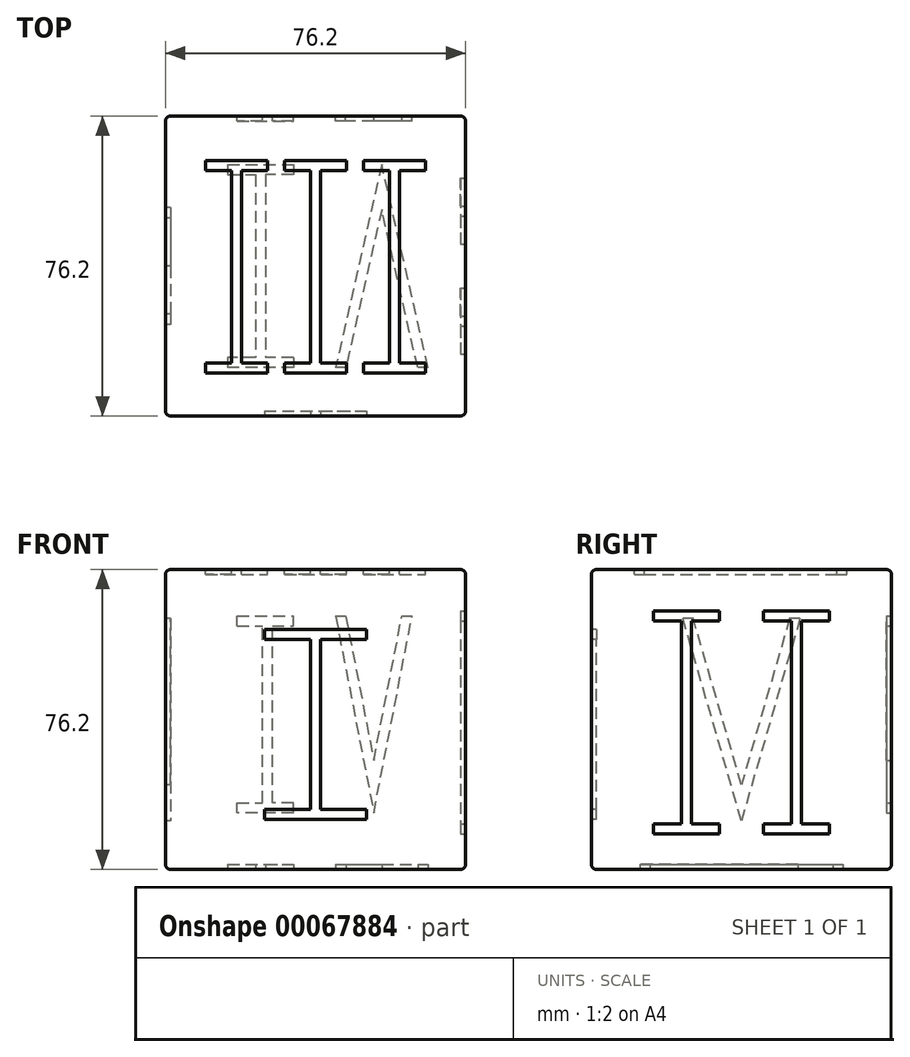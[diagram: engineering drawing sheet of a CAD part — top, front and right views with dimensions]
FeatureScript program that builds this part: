
annotation { "Feature Type Name" : "Feature", "Feature Type Description" : "" }
export const myFeature = defineFeature(function(context is Context, id is Id, definition is map)
    precondition{}
    {
        {
            var Q0;
            Q0=qCreatedBy(makeId("Top.planeOp"),FACE);
            var sketch = newSketch(context, id + "F0", { "sketchPlane" : qUnion([Q0])});
            skLineSegment(sketch, "E0.rect.bottom", {"start": v(38.1, -38.1) * mm, "end": v(-38.1, -38.1) * mm});
            skLineSegment(sketch, "E0.rect.top", {"start": v(38.1, 38.1) * mm, "end": v(-38.1, 38.1) * mm});
            skLineSegment(sketch, "E0.rect.left", {"start": v(38.1, -38.1) * mm, "end": v(38.1, 38.1) * mm});
            skLineSegment(sketch, "E0.rect.right", {"start": v(-38.1, -38.1) * mm, "end": v(-38.1, 38.1) * mm});
            skPoint(sketch, "E0.rect.middle", {"position": v(0, 0) * mm});
            skSolve(sketch);
        }
        {
            var Q0;
            Q0=makeQuery(id+"F0.imprint","IMPRINT",FACE,{"disambiguationData":[TD([[makeQuery(id+"F0.imprint","IMPRINT",EDGE,{"derivedFrom":sQuery(id+"F0.wireOp",EDGE,"E0.rect.bottom")}),-1.0]])]});
            extrude(context, id + "F1", {"entities" : qUnion([Q0]), "endBound" : BoundingType.SYMMETRIC, "depth" : 76.2 * mm});
        }
        {
            var Q0;
            Q0=makeQuery(id+"F1.opExtrude","SWEPT_FACE",FACE,{"disambiguationData":[OSD([sQuery(id+"F0.wireOp",EDGE,"E0.rect.bottom")])]});
            var sketch = newSketch(context, id + "F2", { "sketchPlane" : qUnion([Q0])});
            skLineSegment(sketch, "E1", {"start": v(-13, 22.9) * mm, "end": v(0, 22.9) * mm});
            skLineSegment(sketch, "E2", {"start": v(0, 22.9) * mm, "end": v(13, 22.9) * mm});
            skLineSegment(sketch, "E3", {"start": v(0, 22.9) * mm, "end": v(0, 0) * mm, "construction": true});
            skLineSegment(sketch, "E4.MirrorCS", {"start": v(-13, -22.9) * mm, "end": v(0, -22.9) * mm});
            skLineSegment(sketch, "E5.MirrorCS", {"start": v(0, -22.9) * mm, "end": v(13, -22.9) * mm});
            skLineSegment(sketch, "E6.MirrorCS", {"start": v(0, -22.9) * mm, "end": v(0, 0) * mm, "construction": true});
            skLineSegment(sketch, "E7.0", {"start": v(0, 20.36) * mm, "end": v(13, 20.36) * mm});
            skLineSegment(sketch, "E7.1", {"start": v(-13, 20.36) * mm, "end": v(0, 20.36) * mm});
            skLineSegment(sketch, "E8.0", {"start": v(0, -25.44) * mm, "end": v(13, -25.44) * mm});
            skLineSegment(sketch, "E8.1", {"start": v(-13, -25.44) * mm, "end": v(0, -25.44) * mm});
            skLineSegment(sketch, "E9.0", {"start": v(-1.27, -22.9) * mm, "end": v(-1.27, 0) * mm});
            skLineSegment(sketch, "E9.1", {"start": v(-1.27, 22.9) * mm, "end": v(-1.27, 0) * mm});
            skLineSegment(sketch, "E10.0", {"start": v(1.27, -22.9) * mm, "end": v(1.27, 0) * mm});
            skLineSegment(sketch, "E10.1", {"start": v(1.27, 22.9) * mm, "end": v(1.27, 0) * mm});
            skLineSegment(sketch, "E11", {"start": v(-13, 22.9) * mm, "end": v(-13, 20.36) * mm});
            skLineSegment(sketch, "E12", {"start": v(13, 22.9) * mm, "end": v(13, 20.36) * mm});
            skLineSegment(sketch, "E13", {"start": v(13, -22.9) * mm, "end": v(13, -25.44) * mm});
            skLineSegment(sketch, "E14", {"start": v(-13, -25.44) * mm, "end": v(-13, -22.9) * mm});
            skSolve(sketch);
        }
        {
            var Q0;
            Q0 = qSketchRegion(id + "F2", true);
            extrude(context, id + "F3", {"entities" : qUnion([Q0]), "operationType" : NewBodyOperationType.REMOVE, "endBound" : BoundingType.SYMMETRIC, "oppositeDirection" : true, "depth" : 2.54 * mm});
        }
        {
            var Q0;
            Q0=makeQuery(id+"F1.opExtrude","SWEPT_FACE",FACE,{"disambiguationData":[OSD([sQuery(id+"F0.wireOp",EDGE,"E0.rect.top")])]});
            var sketch = newSketch(context, id + "F4", { "sketchPlane" : qUnion([Q0])});
            skLineSegment(sketch, "E15", {"start": v(-23.23, 26.29) * mm, "end": v(-14.8, -17.08) * mm, "construction": true});
            skLineSegment(sketch, "E16", {"start": v(-14.8, -17.08) * mm, "end": v(-6.37, 26.29) * mm, "construction": true});
            skLineSegment(sketch, "E17", {"start": v(5.59, 23.75) * mm, "end": v(12.23, 23.75) * mm});
            skLineSegment(sketch, "E18", {"start": v(12.23, 23.75) * mm, "end": v(19.96, 23.75) * mm});
            skLineSegment(sketch, "E19", {"start": v(12.23, 23.75) * mm, "end": v(12.23, -21.2) * mm, "construction": true});
            skLineSegment(sketch, "E20", {"start": v(12.23, -21.2) * mm, "end": v(5.59, -21.2) * mm});
            skLineSegment(sketch, "E21", {"start": v(12.23, -21.2) * mm, "end": v(19.96, -21.2) * mm});
            skLineSegment(sketch, "E22.0", {"start": v(-14.8, -10.43) * mm, "end": v(-7.67, 26.29) * mm});
            skLineSegment(sketch, "E22.1", {"start": v(-21.94, 26.29) * mm, "end": v(-14.8, -10.43) * mm});
            skLineSegment(sketch, "E23.0", {"start": v(12.23, 26.29) * mm, "end": v(19.96, 26.29) * mm});
            skLineSegment(sketch, "E23.1", {"start": v(5.59, 26.29) * mm, "end": v(12.23, 26.29) * mm});
            skLineSegment(sketch, "E24.0", {"start": v(12.23, -23.74) * mm, "end": v(5.59, -23.74) * mm});
            skLineSegment(sketch, "E24.1", {"start": v(12.23, -23.74) * mm, "end": v(19.96, -23.74) * mm});
            skLineSegment(sketch, "E25.0", {"start": v(10.96, 23.75) * mm, "end": v(10.96, -21.2) * mm});
            skLineSegment(sketch, "E26.0", {"start": v(13.5, 23.75) * mm, "end": v(13.5, -21.2) * mm});
            skLineSegment(sketch, "E27", {"start": v(5.59, 26.29) * mm, "end": v(5.59, 23.75) * mm});
            skLineSegment(sketch, "E28", {"start": v(19.96, 26.29) * mm, "end": v(19.96, 23.75) * mm});
            skLineSegment(sketch, "E29", {"start": v(19.96, -21.2) * mm, "end": v(19.96, -23.74) * mm});
            skLineSegment(sketch, "E30", {"start": v(5.59, -21.2) * mm, "end": v(5.59, -23.74) * mm});
            skLineSegment(sketch, "E31.0", {"start": v(-14.8, -23.74) * mm, "end": v(-5.08, 26.29) * mm});
            skLineSegment(sketch, "E31.1", {"start": v(-24.53, 26.29) * mm, "end": v(-14.8, -23.74) * mm});
            skLineSegment(sketch, "E32", {"start": v(-24.53, 26.29) * mm, "end": v(-21.94, 26.29) * mm});
            skLineSegment(sketch, "E33", {"start": v(-7.67, 26.29) * mm, "end": v(-5.08, 26.29) * mm});
            skSolve(sketch);
        }
        {
            var Q0;
            Q0 = qSketchRegion(id + "F4", true);
            extrude(context, id + "F5", {"entities" : qUnion([Q0]), "operationType" : NewBodyOperationType.REMOVE, "endBound" : BoundingType.SYMMETRIC, "oppositeDirection" : true, "depth" : 2.54 * mm});
        }
        {
            var Q0;
            Q0=makeQuery(id+"F1.opExtrude","SWEPT_FACE",FACE,{"disambiguationData":[OSD([sQuery(id+"F0.wireOp",EDGE,"E0.rect.right")])]});
            var sketch = newSketch(context, id + "F6", { "sketchPlane" : qUnion([Q0])});
            skLineSegment(sketch, "E34", {"start": v(-12.58, 22.26) * mm, "end": v(0, -21.16) * mm, "construction": true});
            skLineSegment(sketch, "E35", {"start": v(0, -21.16) * mm, "end": v(12.58, 22.26) * mm, "construction": true});
            skLineSegment(sketch, "E36.0", {"start": v(0, -25.72) * mm, "end": v(14.89, 25.65) * mm});
            skLineSegment(sketch, "E36.1", {"start": v(-14.89, 25.65) * mm, "end": v(0, -25.72) * mm});
            skLineSegment(sketch, "E37.0", {"start": v(0, -16.6) * mm, "end": v(12.24, 25.65) * mm});
            skLineSegment(sketch, "E37.1", {"start": v(-12.24, 25.65) * mm, "end": v(0, -16.6) * mm});
            skLineSegment(sketch, "E38", {"start": v(-14.89, 25.65) * mm, "end": v(-12.24, 25.65) * mm});
            skLineSegment(sketch, "E39", {"start": v(12.24, 25.65) * mm, "end": v(14.89, 25.65) * mm});
            skSolve(sketch);
        }
        {
            var Q0;
            Q0 = qSketchRegion(id + "F6", true);
            extrude(context, id + "F7", {"entities" : qUnion([Q0]), "operationType" : NewBodyOperationType.REMOVE, "endBound" : BoundingType.SYMMETRIC, "oppositeDirection" : true, "depth" : 2.54 * mm});
        }
        {
            var Q0;
            Q0=makeQuery(id+"F1.opExtrude","SWEPT_FACE",FACE,{"disambiguationData":[OSD([sQuery(id+"F0.wireOp",EDGE,"E0.rect.left")])]});
            var sketch = newSketch(context, id + "F8", { "sketchPlane" : qUnion([Q0])});
            skLineSegment(sketch, "E40", {"start": v(-22.35, 24.97) * mm, "end": v(-13.97, 24.97) * mm});
            skLineSegment(sketch, "E41", {"start": v(-13.97, 24.97) * mm, "end": v(-5.59, 24.97) * mm});
            skLineSegment(sketch, "E42", {"start": v(-13.97, 24.97) * mm, "end": v(-13.97, -26.48) * mm, "construction": true});
            skLineSegment(sketch, "E43", {"start": v(-13.97, -26.48) * mm, "end": v(-22.35, -26.48) * mm});
            skLineSegment(sketch, "E44", {"start": v(-13.97, -26.48) * mm, "end": v(-5.59, -26.48) * mm});
            skLineSegment(sketch, "E45.0", {"start": v(-13.97, 27.51) * mm, "end": v(-5.59, 27.51) * mm});
            skLineSegment(sketch, "E45.1", {"start": v(-22.35, 27.51) * mm, "end": v(-13.97, 27.51) * mm});
            skLineSegment(sketch, "E46.0", {"start": v(-13.97, -29.02) * mm, "end": v(-22.35, -29.02) * mm});
            skLineSegment(sketch, "E46.1", {"start": v(-13.97, -29.02) * mm, "end": v(-5.59, -29.02) * mm});
            skLineSegment(sketch, "E47.0", {"start": v(-15.24, 24.97) * mm, "end": v(-15.24, -26.48) * mm});
            skLineSegment(sketch, "E48.0", {"start": v(-12.7, 24.97) * mm, "end": v(-12.7, -26.48) * mm});
            skLineSegment(sketch, "E49", {"start": v(-22.35, 27.51) * mm, "end": v(-22.35, 24.97) * mm});
            skLineSegment(sketch, "E50", {"start": v(-5.59, 27.51) * mm, "end": v(-5.59, 24.97) * mm});
            skLineSegment(sketch, "E51", {"start": v(-22.35, -29.02) * mm, "end": v(-22.35, -26.48) * mm});
            skLineSegment(sketch, "E52", {"start": v(-5.59, -26.48) * mm, "end": v(-5.59, -29.02) * mm});
            skLineSegment(sketch, "E53.MirrorCS", {"start": v(12.7, 24.97) * mm, "end": v(12.7, -26.48) * mm});
            skLineSegment(sketch, "E54.MirrorCS", {"start": v(13.97, 24.97) * mm, "end": v(5.59, 24.97) * mm});
            skLineSegment(sketch, "E55.MirrorCS", {"start": v(5.59, 27.51) * mm, "end": v(5.59, 24.97) * mm});
            skLineSegment(sketch, "E56.MirrorCS", {"start": v(13.97, 27.51) * mm, "end": v(5.59, 27.51) * mm});
            skLineSegment(sketch, "E57.MirrorCS", {"start": v(22.35, 27.51) * mm, "end": v(13.97, 27.51) * mm});
            skLineSegment(sketch, "E58.MirrorCS", {"start": v(22.35, 27.51) * mm, "end": v(22.35, 24.97) * mm});
            skLineSegment(sketch, "E59.MirrorCS", {"start": v(15.24, 24.97) * mm, "end": v(15.24, -26.48) * mm});
            skLineSegment(sketch, "E60.MirrorCS", {"start": v(13.97, -26.48) * mm, "end": v(22.35, -26.48) * mm});
            skLineSegment(sketch, "E61.MirrorCS", {"start": v(13.97, -26.48) * mm, "end": v(5.59, -26.48) * mm});
            skLineSegment(sketch, "E62.MirrorCS", {"start": v(13.97, -29.02) * mm, "end": v(5.59, -29.02) * mm});
            skLineSegment(sketch, "E63.MirrorCS", {"start": v(5.59, -26.48) * mm, "end": v(5.59, -29.02) * mm});
            skLineSegment(sketch, "E64.MirrorCS", {"start": v(22.35, -29.02) * mm, "end": v(22.35, -26.48) * mm});
            skLineSegment(sketch, "E65.MirrorCS", {"start": v(13.97, -29.02) * mm, "end": v(22.35, -29.02) * mm});
            skLineSegment(sketch, "E66.MirrorCS", {"start": v(22.35, 24.97) * mm, "end": v(13.97, 24.97) * mm});
            skSolve(sketch);
        }
        {
            var Q0;
            Q0 = qSketchRegion(id + "F8", true);
            extrude(context, id + "F9", {"entities" : qUnion([Q0]), "operationType" : NewBodyOperationType.REMOVE, "endBound" : BoundingType.SYMMETRIC, "oppositeDirection" : true, "depth" : 2.54 * mm});
        }
        {
            var Q0;
            Q0=makeQuery(id+"F1.opExtrude","CAP_FACE",FACE,{"disambiguationData":[OSD([sQuery(id+"F0.wireOp",EDGE,"E0.rect.bottom"),sQuery(id+"F0.wireOp",EDGE,"E0.rect.top"),sQuery(id+"F0.wireOp",EDGE,"E0.rect.left"),sQuery(id+"F0.wireOp",EDGE,"E0.rect.right")])],"isStart":true});
            var sketch = newSketch(context, id + "F10", { "sketchPlane" : qUnion([Q0])});
            skLineSegment(sketch, "E67", {"start": v(-22.35, 23.28) * mm, "end": v(-13.97, 23.28) * mm});
            skLineSegment(sketch, "E68", {"start": v(-13.97, 23.28) * mm, "end": v(-5.59, 23.28) * mm});
            skLineSegment(sketch, "E69", {"start": v(-13.97, -23.2) * mm, "end": v(-22.35, -23.2) * mm});
            skLineSegment(sketch, "E70", {"start": v(-13.97, -23.2) * mm, "end": v(-5.59, -23.2) * mm});
            skLineSegment(sketch, "E71", {"start": v(-13.97, 23.28) * mm, "end": v(-13.97, -23.2) * mm, "construction": true});
            skLineSegment(sketch, "E72", {"start": v(6.38, 25.82) * mm, "end": v(16.83, -20.02) * mm, "construction": true});
            skLineSegment(sketch, "E73", {"start": v(16.83, -20.02) * mm, "end": v(27.28, 25.82) * mm, "construction": true});
            skLineSegment(sketch, "E74.0", {"start": v(-13.97, 25.82) * mm, "end": v(-5.59, 25.82) * mm});
            skLineSegment(sketch, "E74.1", {"start": v(-22.35, 25.82) * mm, "end": v(-13.97, 25.82) * mm});
            skLineSegment(sketch, "E75.0", {"start": v(-13.97, -25.73) * mm, "end": v(-22.35, -25.73) * mm});
            skLineSegment(sketch, "E75.1", {"start": v(-13.97, -25.73) * mm, "end": v(-5.59, -25.73) * mm});
            skLineSegment(sketch, "E76.0", {"start": v(-15.24, 23.28) * mm, "end": v(-15.24, -23.2) * mm});
            skLineSegment(sketch, "E77.0", {"start": v(-12.7, 23.28) * mm, "end": v(-12.7, -23.2) * mm});
            skLineSegment(sketch, "E78.0", {"start": v(16.83, -25.73) * mm, "end": v(28.58, 25.82) * mm});
            skLineSegment(sketch, "E78.1", {"start": v(5.08, 25.82) * mm, "end": v(16.83, -25.73) * mm});
            skLineSegment(sketch, "E79.0", {"start": v(16.83, -14.3) * mm, "end": v(25.97, 25.82) * mm});
            skLineSegment(sketch, "E79.1", {"start": v(7.69, 25.82) * mm, "end": v(16.83, -14.3) * mm});
            skLineSegment(sketch, "E80", {"start": v(-22.35, 25.82) * mm, "end": v(-22.35, 23.28) * mm});
            skLineSegment(sketch, "E81", {"start": v(-5.59, 25.82) * mm, "end": v(-5.59, 23.28) * mm});
            skLineSegment(sketch, "E82", {"start": v(-22.35, -23.2) * mm, "end": v(-22.35, -25.73) * mm});
            skLineSegment(sketch, "E83", {"start": v(-5.59, -23.2) * mm, "end": v(-5.59, -25.73) * mm});
            skLineSegment(sketch, "E84", {"start": v(5.08, 25.82) * mm, "end": v(7.69, 25.82) * mm});
            skLineSegment(sketch, "E85", {"start": v(25.97, 25.82) * mm, "end": v(28.58, 25.82) * mm});
            skSolve(sketch);
        }
        {
            var Q0;
            Q0 = qSketchRegion(id + "F10", true);
            extrude(context, id + "F11", {"entities" : qUnion([Q0]), "operationType" : NewBodyOperationType.REMOVE, "endBound" : BoundingType.SYMMETRIC, "oppositeDirection" : true, "depth" : 2.54 * mm});
        }
        {
            var Q0;
            Q0=makeQuery(id+"F1.opExtrude","CAP_FACE",FACE,{"disambiguationData":[OSD([sQuery(id+"F0.wireOp",EDGE,"E0.rect.bottom"),sQuery(id+"F0.wireOp",EDGE,"E0.rect.top"),sQuery(id+"F0.wireOp",EDGE,"E0.rect.left"),sQuery(id+"F0.wireOp",EDGE,"E0.rect.right")])],"isStart":false});
            var sketch = newSketch(context, id + "F12", { "sketchPlane" : qUnion([Q0])});
            skLineSegment(sketch, "E86", {"start": v(27.9, -24.69) * mm, "end": v(20.05, -24.69) * mm});
            skLineSegment(sketch, "E87", {"start": v(20.05, -24.69) * mm, "end": v(12.22, -24.69) * mm});
            skLineSegment(sketch, "E88", {"start": v(20.05, -24.69) * mm, "end": v(20.05, 24.25) * mm, "construction": true});
            skLineSegment(sketch, "E89", {"start": v(20.05, 24.25) * mm, "end": v(27.9, 24.25) * mm});
            skLineSegment(sketch, "E90", {"start": v(20.05, 24.25) * mm, "end": v(12.22, 24.25) * mm});
            skLineSegment(sketch, "E91", {"start": v(7.84, -24.69) * mm, "end": v(0, -24.69) * mm});
            skLineSegment(sketch, "E92", {"start": v(0, -24.69) * mm, "end": v(0, 24.25) * mm, "construction": true});
            skLineSegment(sketch, "E93", {"start": v(0, 24.25) * mm, "end": v(7.84, 24.25) * mm});
            skLineSegment(sketch, "E94.0", {"start": v(20.05, -27.23) * mm, "end": v(12.22, -27.23) * mm});
            skLineSegment(sketch, "E94.1", {"start": v(27.9, -27.23) * mm, "end": v(20.05, -27.23) * mm});
            skLineSegment(sketch, "E95.0", {"start": v(20.05, 26.79) * mm, "end": v(27.9, 26.79) * mm});
            skLineSegment(sketch, "E95.1", {"start": v(20.05, 26.79) * mm, "end": v(12.22, 26.79) * mm});
            skLineSegment(sketch, "E96.0", {"start": v(0, 26.79) * mm, "end": v(7.84, 26.79) * mm});
            skLineSegment(sketch, "E97.0", {"start": v(7.84, -27.23) * mm, "end": v(0, -27.23) * mm});
            skLineSegment(sketch, "E98.0", {"start": v(21.32, -24.69) * mm, "end": v(21.32, 24.25) * mm});
            skLineSegment(sketch, "E99.0", {"start": v(18.78, -24.69) * mm, "end": v(18.78, 24.25) * mm});
            skLineSegment(sketch, "E100.0", {"start": v(1.27, -24.69) * mm, "end": v(1.27, 24.25) * mm});
            skLineSegment(sketch, "E101", {"start": v(7.84, -27.23) * mm, "end": v(7.84, -24.69) * mm});
            skLineSegment(sketch, "E102", {"start": v(12.22, -27.23) * mm, "end": v(12.22, -24.69) * mm});
            skLineSegment(sketch, "E103", {"start": v(27.9, -27.23) * mm, "end": v(27.9, -24.69) * mm});
            skLineSegment(sketch, "E104", {"start": v(27.9, 24.25) * mm, "end": v(27.9, 26.79) * mm});
            skLineSegment(sketch, "E105", {"start": v(12.22, 24.25) * mm, "end": v(12.22, 26.79) * mm});
            skLineSegment(sketch, "E106", {"start": v(7.84, 24.25) * mm, "end": v(7.84, 26.79) * mm});
            skPoint(sketch, "E107", {"position": v(3.92, -24.69) * mm});
            skLineSegment(sketch, "E108.MirrorCS", {"start": v(0, 26.79) * mm, "end": v(-7.84, 26.79) * mm});
            skLineSegment(sketch, "E109.MirrorCS", {"start": v(-7.84, 24.25) * mm, "end": v(-7.84, 26.79) * mm});
            skLineSegment(sketch, "E110.MirrorCS", {"start": v(0, 24.25) * mm, "end": v(-7.84, 24.25) * mm});
            skLineSegment(sketch, "E111.MirrorCS", {"start": v(-1.27, -24.69) * mm, "end": v(-1.27, 24.25) * mm});
            skLineSegment(sketch, "E112.MirrorCS", {"start": v(-7.84, -24.69) * mm, "end": v(0, -24.69) * mm});
            skLineSegment(sketch, "E113.MirrorCS", {"start": v(-7.84, -27.23) * mm, "end": v(-7.84, -24.69) * mm});
            skLineSegment(sketch, "E114.MirrorCS", {"start": v(-7.84, -27.23) * mm, "end": v(0, -27.23) * mm});
            skLineSegment(sketch, "E115.MirrorCS", {"start": v(-12.22, -27.23) * mm, "end": v(-12.22, -24.69) * mm});
            skLineSegment(sketch, "E116.MirrorCS", {"start": v(-20.05, -27.23) * mm, "end": v(-12.22, -27.23) * mm});
            skLineSegment(sketch, "E117.MirrorCS", {"start": v(-27.9, -27.23) * mm, "end": v(-20.05, -27.23) * mm});
            skLineSegment(sketch, "E118.MirrorCS", {"start": v(-27.9, -24.69) * mm, "end": v(-20.05, -24.69) * mm});
            skLineSegment(sketch, "E119.MirrorCS", {"start": v(-20.05, -24.69) * mm, "end": v(-12.22, -24.69) * mm});
            skLineSegment(sketch, "E120.MirrorCS", {"start": v(-18.78, -24.69) * mm, "end": v(-18.78, 24.25) * mm});
            skLineSegment(sketch, "E121.MirrorCS", {"start": v(-21.32, -24.69) * mm, "end": v(-21.32, 24.25) * mm});
            skLineSegment(sketch, "E122.MirrorCS", {"start": v(-27.9, -27.23) * mm, "end": v(-27.9, -24.69) * mm});
            skLineSegment(sketch, "E123.MirrorCS", {"start": v(-20.05, 24.25) * mm, "end": v(-27.9, 24.25) * mm});
            skLineSegment(sketch, "E124.MirrorCS", {"start": v(-27.9, 24.25) * mm, "end": v(-27.9, 26.79) * mm});
            skLineSegment(sketch, "E125.MirrorCS", {"start": v(-20.05, 26.79) * mm, "end": v(-27.9, 26.79) * mm});
            skLineSegment(sketch, "E126.MirrorCS", {"start": v(-20.05, 26.79) * mm, "end": v(-12.22, 26.79) * mm});
            skLineSegment(sketch, "E127.MirrorCS", {"start": v(-12.22, 24.25) * mm, "end": v(-12.22, 26.79) * mm});
            skLineSegment(sketch, "E128.MirrorCS", {"start": v(-20.05, 24.25) * mm, "end": v(-12.22, 24.25) * mm});
            skSolve(sketch);
        }
        {
            var Q0;
            Q0 = qSketchRegion(id + "F12", true);
            extrude(context, id + "F13", {"entities" : qUnion([Q0]), "operationType" : NewBodyOperationType.REMOVE, "endBound" : BoundingType.SYMMETRIC, "oppositeDirection" : true, "depth" : 2.54 * mm});
        }
        {
            var Q0;
            Q0=makeQuery(id+"F1.opExtrude","CAP_EDGE",EDGE,{"disambiguationData":[OSD([sQuery(id+"F0.wireOp",EDGE,"E0.rect.left")])],"isStart":false});
            var Q1;
            Q1=makeQuery(id+"F1.opExtrude","CAP_EDGE",EDGE,{"disambiguationData":[OSD([sQuery(id+"F0.wireOp",EDGE,"E0.rect.bottom")])],"isStart":false});
            var Q2;
            Q2=makeQuery(id+"F1.opExtrude","CAP_EDGE",EDGE,{"disambiguationData":[OSD([sQuery(id+"F0.wireOp",EDGE,"E0.rect.right")])],"isStart":false});
            var Q3;
            Q3=makeQuery(id+"F1.opExtrude","CAP_EDGE",EDGE,{"disambiguationData":[OSD([sQuery(id+"F0.wireOp",EDGE,"E0.rect.top")])],"isStart":false});
            var Q4;
            Q4=makeQuery(id+"F1.opExtrude","SWEPT_EDGE",EDGE,{"disambiguationData":[OSD([sQuery(id+"F0.wireOp",EDGE,"E0.rect.bottom"),sQuery(id+"F0.wireOp",EDGE,"E0.rect.right")])]});
            var Q5;
            Q5=makeQuery(id+"F1.opExtrude","CAP_EDGE",EDGE,{"disambiguationData":[OSD([sQuery(id+"F0.wireOp",EDGE,"E0.rect.bottom")])],"isStart":true});
            var Q6;
            Q6=makeQuery(id+"F1.opExtrude","SWEPT_EDGE",EDGE,{"disambiguationData":[OSD([sQuery(id+"F0.wireOp",EDGE,"E0.rect.bottom"),sQuery(id+"F0.wireOp",EDGE,"E0.rect.left")])]});
            var Q7;
            Q7=makeQuery(id+"F1.opExtrude","CAP_EDGE",EDGE,{"disambiguationData":[OSD([sQuery(id+"F0.wireOp",EDGE,"E0.rect.right")])],"isStart":true});
            var Q8;
            Q8=makeQuery(id+"F1.opExtrude","SWEPT_EDGE",EDGE,{"disambiguationData":[OSD([sQuery(id+"F0.wireOp",EDGE,"E0.rect.top"),sQuery(id+"F0.wireOp",EDGE,"E0.rect.right")])]});
            var Q9;
            Q9=makeQuery(id+"F1.opExtrude","SWEPT_EDGE",EDGE,{"disambiguationData":[OSD([sQuery(id+"F0.wireOp",EDGE,"E0.rect.top"),sQuery(id+"F0.wireOp",EDGE,"E0.rect.left")])]});
            var Q10;
            Q10=makeQuery(id+"F1.opExtrude","CAP_EDGE",EDGE,{"disambiguationData":[OSD([sQuery(id+"F0.wireOp",EDGE,"E0.rect.top")])],"isStart":true});
            var Q11;
            Q11=makeQuery(id+"F1.opExtrude","CAP_EDGE",EDGE,{"disambiguationData":[OSD([sQuery(id+"F0.wireOp",EDGE,"E0.rect.left")])],"isStart":true});
            fillet(context, id + "F14", {"entities" : qUnion([Q0, Q1, Q2, Q3, Q4, Q5, Q6, Q7, Q8, Q9, Q10, Q11]), "radius" : 1.27 * mm, "tangentPropagation" : true, "allowEdgeOverflow" : false});
        }
    });
